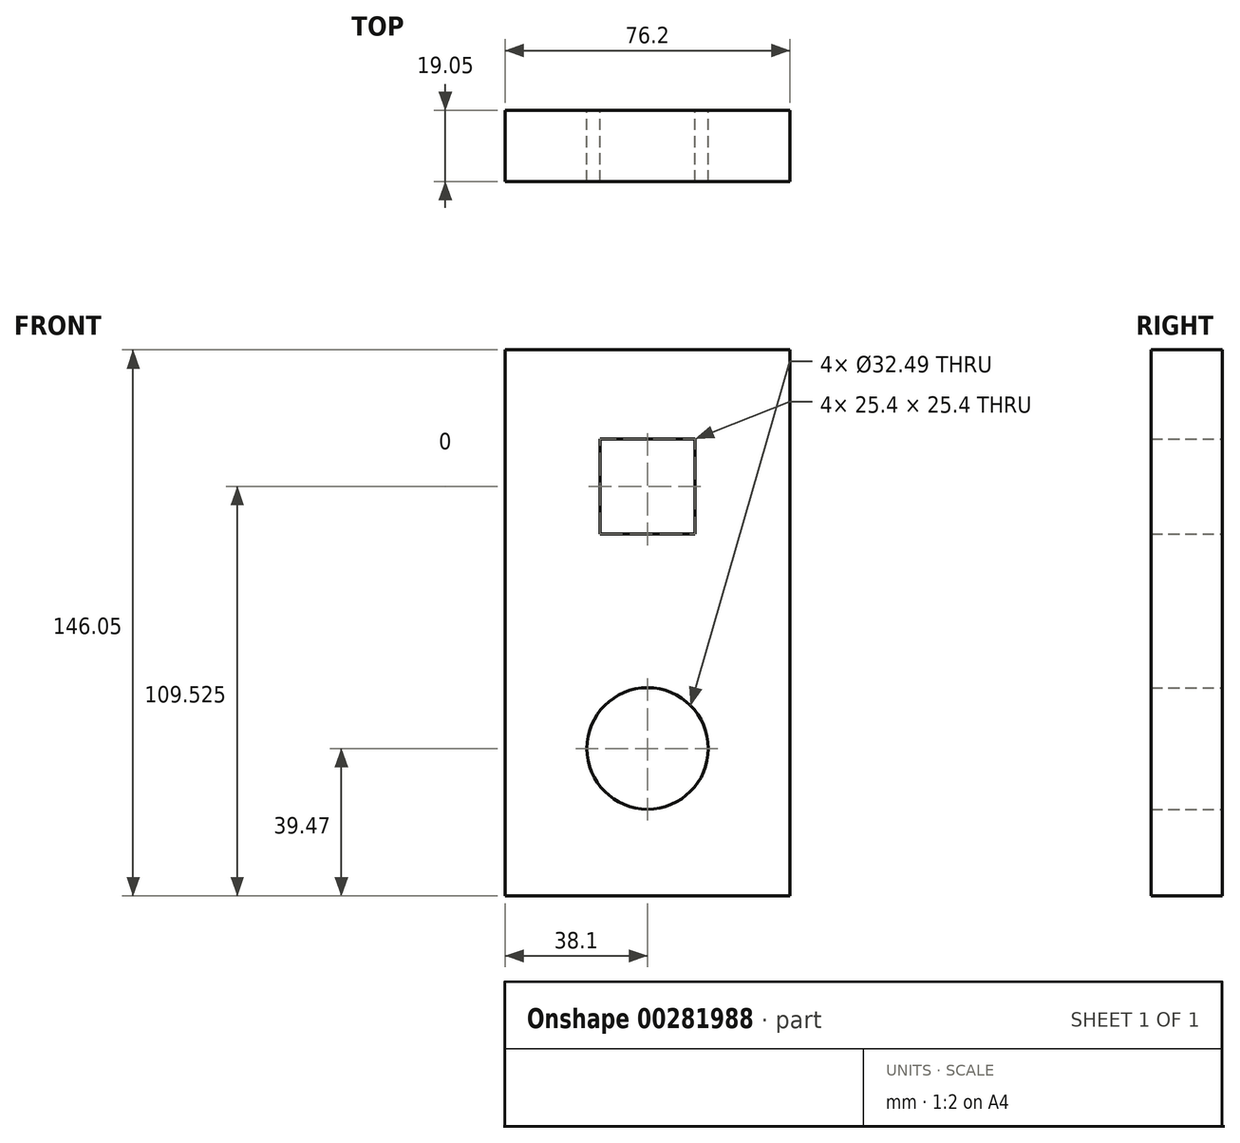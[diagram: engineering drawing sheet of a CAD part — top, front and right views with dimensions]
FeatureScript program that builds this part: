
annotation { "Feature Type Name" : "Feature", "Feature Type Description" : "" }
export const myFeature = defineFeature(function(context is Context, id is Id, definition is map)
    precondition{}
    {
        {
            var Q0;
            Q0=qCreatedBy(makeId("Front.planeOp"),FACE);
            var sketch = newSketch(context, id + "F0", { "sketchPlane" : qUnion([Q0])});
            skLineSegment(sketch, "E0.bottom", {"start": v(0, 0) * mm, "end": v(-76.2, 0) * mm});
            skLineSegment(sketch, "E0.top", {"start": v(0, 146.05) * mm, "end": v(-76.2, 146.05) * mm});
            skLineSegment(sketch, "E0.left", {"start": v(0, 0) * mm, "end": v(0, 146.05) * mm});
            skLineSegment(sketch, "E0.right", {"start": v(-76.2, 0) * mm, "end": v(-76.2, 146.05) * mm});
            skLineSegment(sketch, "E1.bottom", {"start": v(-25.4, 122.22) * mm, "end": v(-50.8, 122.22) * mm});
            skLineSegment(sketch, "E1.top", {"start": v(-25.4, 96.82) * mm, "end": v(-50.8, 96.82) * mm});
            skLineSegment(sketch, "E1.left", {"start": v(-25.4, 122.22) * mm, "end": v(-25.4, 96.82) * mm});
            skLineSegment(sketch, "E1.right", {"start": v(-50.8, 122.22) * mm, "end": v(-50.8, 96.82) * mm});
            skCircle(sketch, "E2", {"center": v(-38.1, 39.47) * mm, "radius": 16.24 * mm});
            skLineSegment(sketch, "E3", {"start": v(0, 75.44) * mm, "end": v(-76.2, 75.44) * mm});
            skSolve(sketch);
        }
        {
            var Q0;
            Q0 = qSketchRegion(id + "F0", true);
            extrude(context, id + "F1", {"entities" : qUnion([Q0]), "depth" : 19.05 * mm});
        }
    });
